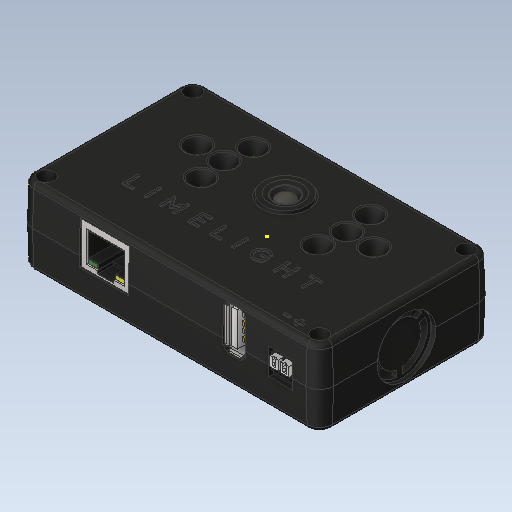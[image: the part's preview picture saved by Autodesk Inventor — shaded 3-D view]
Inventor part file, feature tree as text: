
AUTODESK INVENTOR PART (.ipt)
format: ipt  version: 2020 (Build 240168000, 168)  size: 4,884,992 bytes
history: native  units: in
note: dims shown in document units (in); Inventor stores cm internally (conversion verified against a paired STEP export)
features: other x11, sketch x1
ambient origin geometry x8: Origin, YZ Plane, XZ Plane, XY Plane, X Axis, Y Axis, Z Axis, Center Point
bodies: Solid2 (feature_tree), Solid3 (feature_tree), Solid4 (feature_tree), Solid5 (feature_tree), Solid6 (feature_tree), Solid7 (feature_tree), Solid8 (feature_tree), Solid9 (feature_tree), Solid10 (feature_tree), Solid11 (feature_tree), Solid12 (feature_tree), Solid13 (feature_tree), Solid1 (feature_tree)
feature tree (12):
  sketch  "Sketch1"
  other  "Solid2:1"
  other  "Solid3:1"
  other  "Solid4:1"
  other  "Solid5:1"
  other  "Solid6:1"
  other  "Solid7:1"
  other  "Solid8:1"
  other  "Solid9:1"
  other  "Solid10:1"
  other  "Solid11:1"
  other  "Solid12:1"
